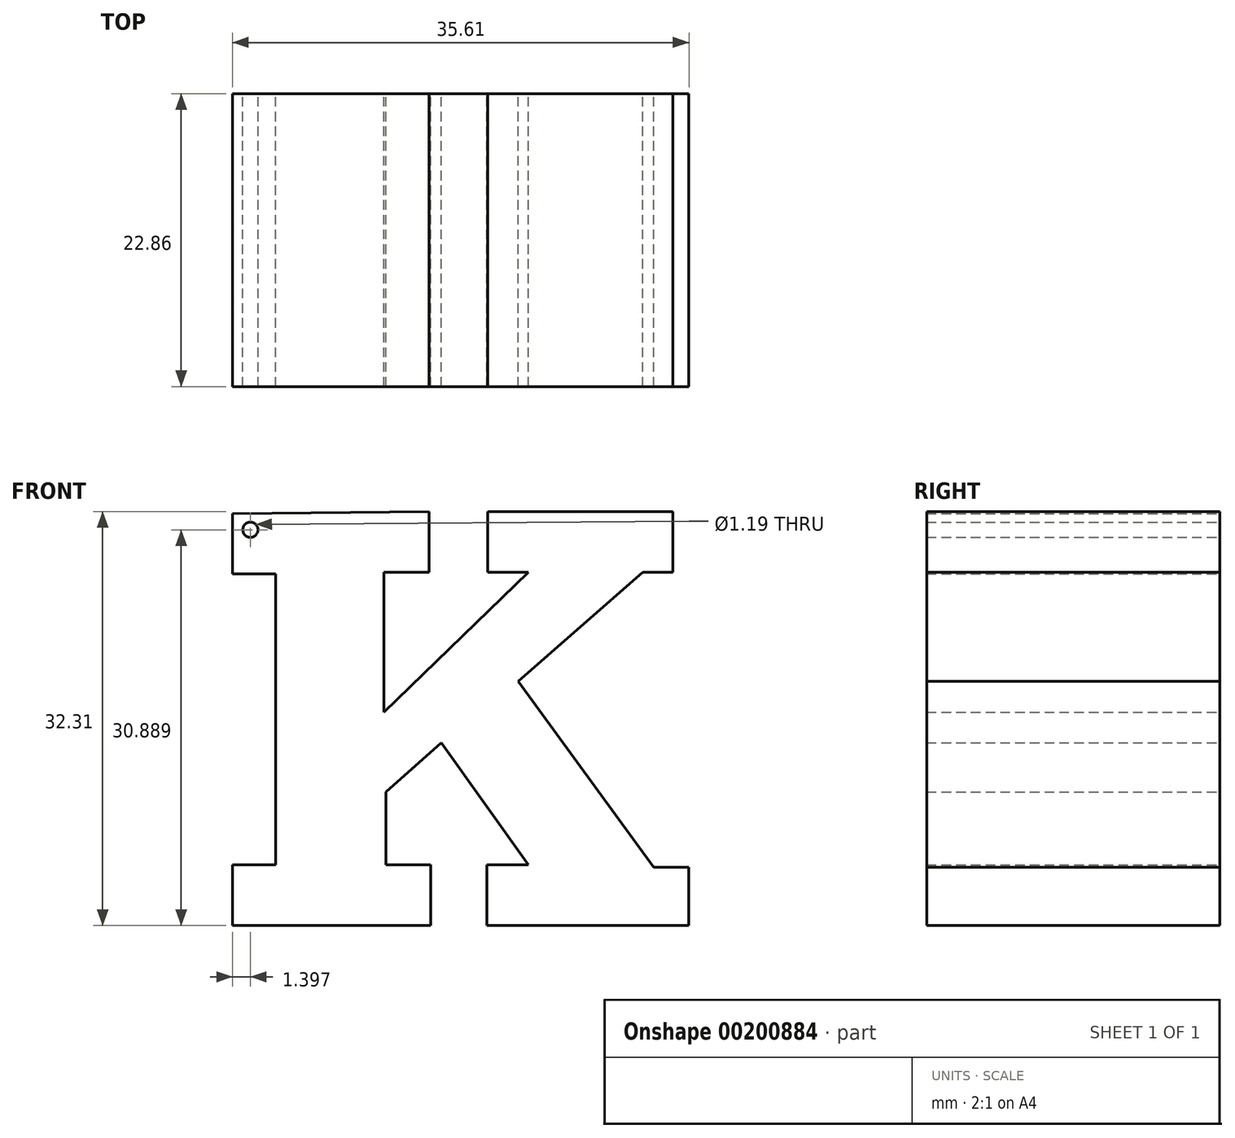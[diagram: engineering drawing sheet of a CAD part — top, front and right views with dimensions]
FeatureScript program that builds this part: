
annotation { "Feature Type Name" : "Feature", "Feature Type Description" : "" }
export const myFeature = defineFeature(function(context is Context, id is Id, definition is map)
    precondition{}
    {
        {
            var Q0;
            Q0=qCreatedBy(makeId("Front.planeOp"),FACE);
            var sketch = newSketch(context, id + "F0", { "sketchPlane" : qUnion([Q0])});
            skLineSegment(sketch, "E0", {"start": v(-111.68, 8.7) * mm, "end": v(-74.3, 8.7) * mm});
            skLineSegment(sketch, "E1", {"start": v(-111.68, 8.7) * mm, "end": v(-111.68, -27.88) * mm});
            skLineSegment(sketch, "E2", {"start": v(-61.24, 6.75) * mm, "end": v(-61.24, 2.08) * mm});
            skLineSegment(sketch, "E3", {"start": v(-61.24, 2.08) * mm, "end": v(-57.89, 2.08) * mm});
            skLineSegment(sketch, "E4", {"start": v(-57.89, 2.08) * mm, "end": v(-57.89, -20.65) * mm});
            skLineSegment(sketch, "E5", {"start": v(-57.89, -20.65) * mm, "end": v(-61.24, -20.65) * mm});
            skLineSegment(sketch, "E6", {"start": v(-61.24, -20.65) * mm, "end": v(-61.24, -25.38) * mm});
            skLineSegment(sketch, "E7", {"start": v(-61.24, -25.38) * mm, "end": v(-45.78, -25.38) * mm});
            skLineSegment(sketch, "E8", {"start": v(-45.78, -25.38) * mm, "end": v(-45.78, -20.65) * mm});
            skLineSegment(sketch, "E9", {"start": v(-45.78, -20.65) * mm, "end": v(-49.25, -20.65) * mm});
            skLineSegment(sketch, "E10", {"start": v(-49.25, -20.65) * mm, "end": v(-49.25, -14.95) * mm});
            skLineSegment(sketch, "E11", {"start": v(-49.25, -14.95) * mm, "end": v(-44.94, -11.11) * mm});
            skLineSegment(sketch, "E12", {"start": v(-44.94, -11.11) * mm, "end": v(-38.16, -20.65) * mm});
            skLineSegment(sketch, "E13", {"start": v(-38.16, -20.65) * mm, "end": v(-41.4, -20.65) * mm});
            skLineSegment(sketch, "E14", {"start": v(-41.4, -20.59) * mm, "end": v(-41.4, -25.38) * mm});
            skLineSegment(sketch, "E15", {"start": v(-41.4, -25.38) * mm, "end": v(-25.63, -25.38) * mm});
            skLineSegment(sketch, "E16", {"start": v(-25.63, -25.38) * mm, "end": v(-25.63, -20.83) * mm});
            skLineSegment(sketch, "E17", {"start": v(-25.63, -20.83) * mm, "end": v(-28.4, -20.83) * mm});
            skLineSegment(sketch, "E18", {"start": v(-28.4, -20.83) * mm, "end": v(-38.94, -6.32) * mm});
            skLineSegment(sketch, "E19", {"start": v(-38.94, -6.32) * mm, "end": v(-29.23, 2.2) * mm});
            skLineSegment(sketch, "E20", {"start": v(-29.23, 2.2) * mm, "end": v(-26.9, 2.2) * mm});
            skLineSegment(sketch, "E21", {"start": v(-26.9, 2.2) * mm, "end": v(-26.9, 6.93) * mm});
            skLineSegment(sketch, "E22", {"start": v(-26.9, 6.93) * mm, "end": v(-41.34, 6.93) * mm});
            skLineSegment(sketch, "E23", {"start": v(-41.34, 6.93) * mm, "end": v(-41.34, 2.2) * mm});
            skLineSegment(sketch, "E24", {"start": v(-41.34, 2.2) * mm, "end": v(-38.16, 2.2) * mm});
            skLineSegment(sketch, "E25", {"start": v(-49.43, -8.72) * mm, "end": v(-49.43, 2.2) * mm});
            skLineSegment(sketch, "E26", {"start": v(-45.9, 2.2) * mm, "end": v(-45.9, 6.93) * mm});
            skLineSegment(sketch, "E27", {"start": v(-45.9, 6.93) * mm, "end": v(-61.24, 6.75) * mm});
            skLineSegment(sketch, "E28", {"start": v(-49.43, 2.2) * mm, "end": v(-45.9, 2.2) * mm});
            skLineSegment(sketch, "E29", {"start": v(-49.43, -8.72) * mm, "end": v(-38.16, 2.2) * mm});
            skCircle(sketch, "E30", {"center": v(-59.84, 5.5) * mm, "radius": 0.6 * mm});
            skSolve(sketch);
        }
        {
            var Q0;
            Q0 = qSketchRegion(id + "F0", true);
            extrude(context, id + "F1", {"entities" : qUnion([Q0]), "depth" : 22.86 * mm});
        }
    });
